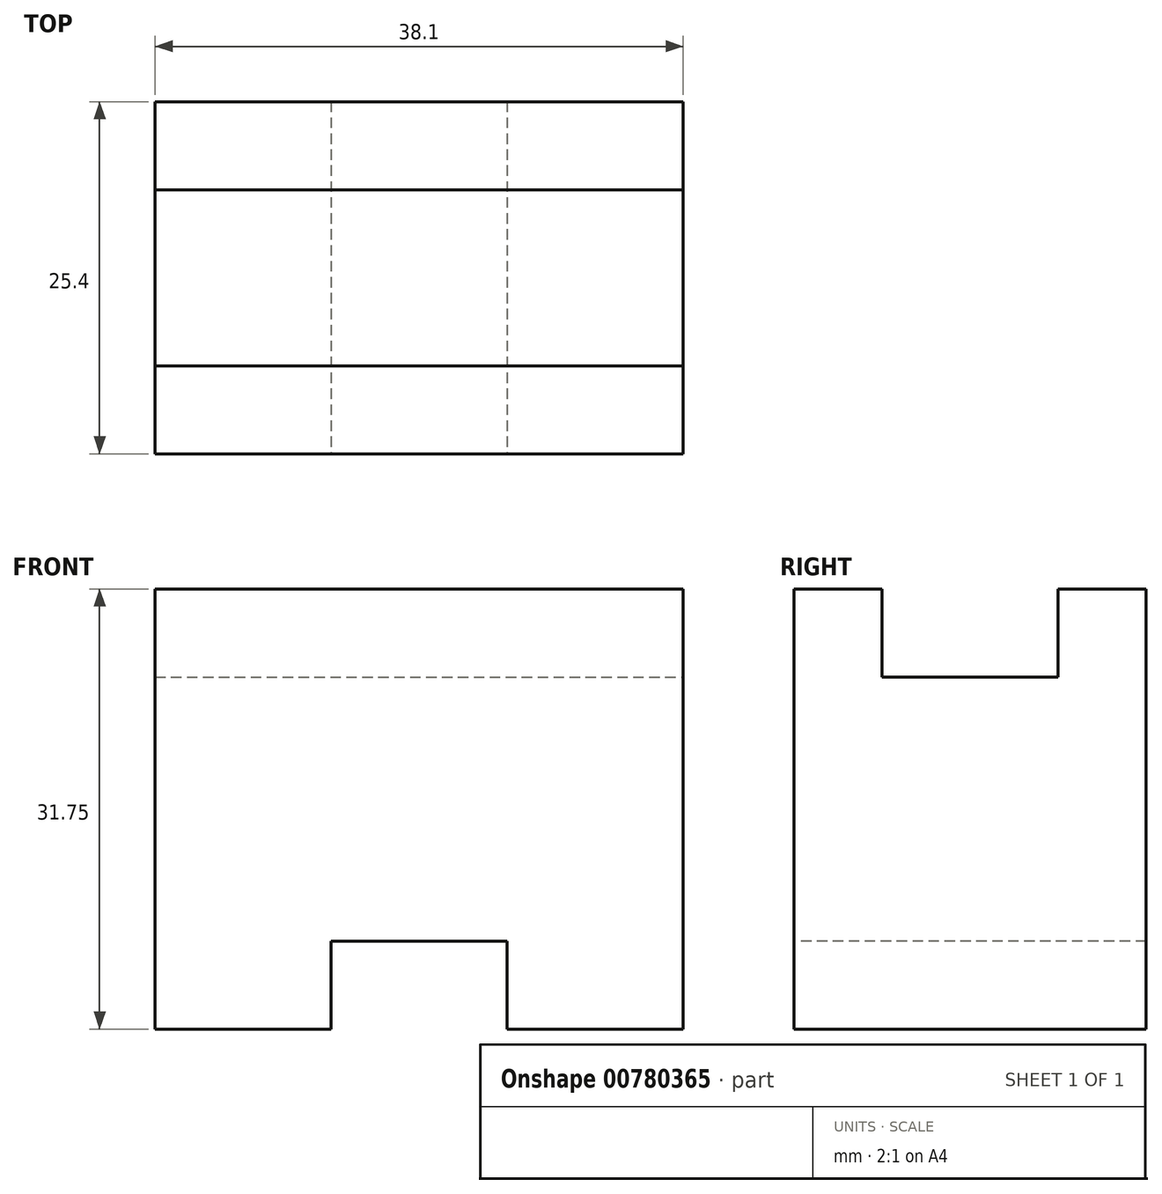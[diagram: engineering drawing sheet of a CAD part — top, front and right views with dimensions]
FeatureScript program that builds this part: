
annotation { "Feature Type Name" : "Feature", "Feature Type Description" : "" }
export const myFeature = defineFeature(function(context is Context, id is Id, definition is map)
    precondition{}
    {
        {
            var Q0;
            Q0=qCreatedBy(makeId("Front.planeOp"),FACE);
            var sketch = newSketch(context, id + "F0", { "sketchPlane" : qUnion([Q0])});
            skLineSegment(sketch, "E0", {"start": v(0, 0) * mm, "end": v(0, 31.75) * mm});
            skLineSegment(sketch, "E1", {"start": v(0, 31.75) * mm, "end": v(38.1, 31.75) * mm});
            skLineSegment(sketch, "E2", {"start": v(38.1, 31.75) * mm, "end": v(38.1, 0) * mm});
            skLineSegment(sketch, "E3", {"start": v(38.1, 0) * mm, "end": v(0, 0) * mm});
            skSolve(sketch);
        }
        {
            var Q0;
            Q0=makeQuery(id+"F0.imprint","IMPRINT",FACE,{"disambiguationData":[TD([[makeQuery(id+"F0.imprint","IMPRINT",EDGE,{"derivedFrom":sQuery(id+"F0.wireOp",EDGE,"E0")}),-1.0]])]});
            extrude(context, id + "F1", {"entities" : qUnion([Q0]), "depth" : 25.4 * mm, "offsetDistance" : 25.4 * mm});
        }
        {
            var Q0;
            Q0=makeQuery(id+"F1.opExtrude","CAP_FACE",FACE,{"disambiguationData":[OSD([sQuery(id+"F0.wireOp",EDGE,"E0"),sQuery(id+"F0.wireOp",EDGE,"E1"),sQuery(id+"F0.wireOp",EDGE,"E2"),sQuery(id+"F0.wireOp",EDGE,"E3")])],"isStart":false});
            var sketch = newSketch(context, id + "F2", { "sketchPlane" : qUnion([Q0])});
            skLineSegment(sketch, "E4", {"start": v(0, 0) * mm, "end": v(12.7, 0) * mm});
            skLineSegment(sketch, "E5", {"start": v(12.7, 0) * mm, "end": v(12.7, 6.35) * mm});
            skLineSegment(sketch, "E6", {"start": v(12.7, 6.35) * mm, "end": v(25.4, 6.35) * mm});
            skLineSegment(sketch, "E7", {"start": v(25.4, 0) * mm, "end": v(25.4, 6.35) * mm});
            skLineSegment(sketch, "E8", {"start": v(25.4, 0) * mm, "end": v(38.1, 0) * mm});
            skSolve(sketch);
        }
        {
            var Q0;
            {var subQ0=sQuery(id+"F2.wireOp",EDGE,"E5");Q0=makeQuery(id+"F2.imprint","IMPRINT",FACE,{"disambiguationData":[TD([[makeQuery(id+"F2.imprint","IMPRINT",EDGE,{"derivedFrom":subQ0}),-1.0]])]});}
            extrude(context, id + "F3", {"entities" : qUnion([Q0]), "operationType" : NewBodyOperationType.REMOVE, "oppositeDirection" : true, "depth" : 25.4 * mm, "offsetDistance" : 25.4 * mm});
        }
        {
            var Q0;
            Q0=makeQuery(id+"F1.opExtrude","SWEPT_FACE",FACE,{"disambiguationData":[OSD([sQuery(id+"F0.wireOp",EDGE,"E2")])]});
            var sketch = newSketch(context, id + "F4", { "sketchPlane" : qUnion([Q0])});
            skLineSegment(sketch, "E9", {"start": v(-25.4, 31.75) * mm, "end": v(-19.05, 31.75) * mm});
            skLineSegment(sketch, "E10", {"start": v(-19.05, 31.75) * mm, "end": v(-19.05, 25.4) * mm});
            skLineSegment(sketch, "E11", {"start": v(-19.05, 25.4) * mm, "end": v(-6.35, 25.4) * mm});
            skLineSegment(sketch, "E12", {"start": v(-6.35, 25.4) * mm, "end": v(-6.35, 31.75) * mm});
            skLineSegment(sketch, "E13", {"start": v(-6.35, 31.75) * mm, "end": v(0, 31.75) * mm});
            skSolve(sketch);
        }
        {
            var Q0;
            {var subQ0=sQuery(id+"F4.wireOp",EDGE,"E10");Q0=makeQuery(id+"F4.imprint","IMPRINT",FACE,{"disambiguationData":[TD([[makeQuery(id+"F4.imprint","IMPRINT",EDGE,{"derivedFrom":subQ0}),1.0]])]});}
            extrude(context, id + "F5", {"entities" : qUnion([Q0]), "operationType" : NewBodyOperationType.REMOVE, "oppositeDirection" : true, "depth" : 25.4 * mm, "offsetDistance" : 25.4 * mm});
        }
        {
            var Q0;
            Q0=makeQuery(id+"F5.boolean.opBoolean","COPY",FACE,{"derivedFrom":makeQuery(id+"F5.opExtrude","CAP_FACE",FACE,{"disambiguationData":[OSD([sQuery(id+"F0.wireOp",EDGE,"E1"),sQuery(id+"F0.wireOp",EDGE,"E2"),sQuery(id+"F4.wireOp",EDGE,"E10"),sQuery(id+"F4.wireOp",EDGE,"E11"),sQuery(id+"F4.wireOp",EDGE,"E12")])],"isStart":false})});
            extrude(context, id + "F6", {"entities" : qUnion([Q0]), "operationType" : NewBodyOperationType.REMOVE, "oppositeDirection" : true, "depth" : 25.4 * mm, "offsetDistance" : 25.4 * mm});
        }
    });
